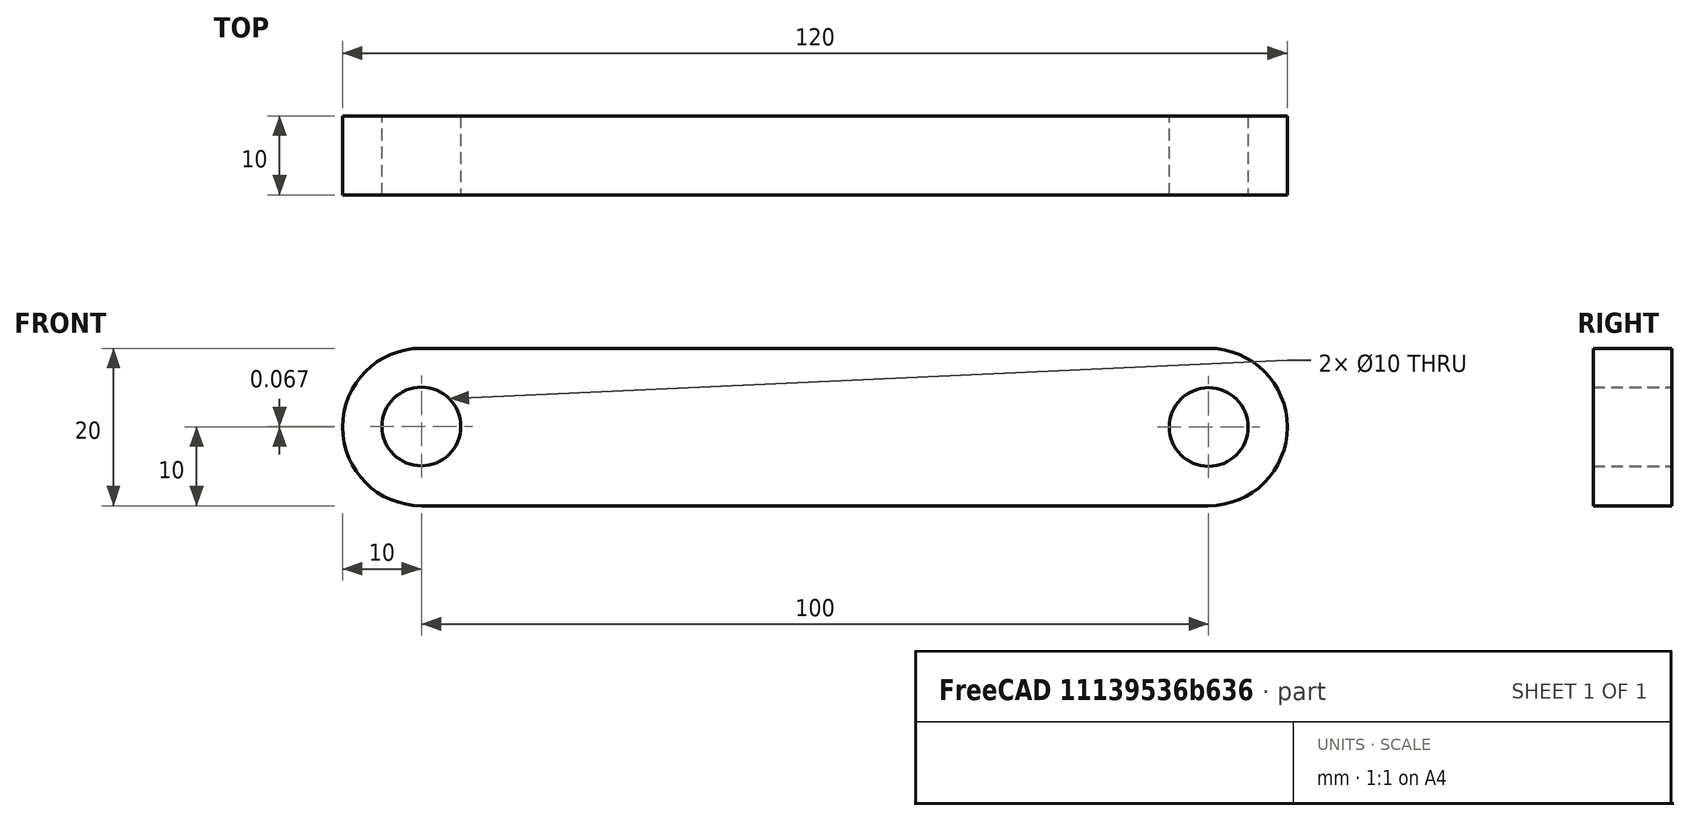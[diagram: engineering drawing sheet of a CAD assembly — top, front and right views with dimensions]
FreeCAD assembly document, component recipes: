
FREECAD ASSEMBLY — COMPONENT RECIPES ("Tuto1-001")

This assembly document has 2 components, labeled P0..P1 below (a component is one placed body or linked part). 1 of them carries a construction recipe — the FreeCAD feature program that regenerates the part from scratch, quoted from this document or its linked companion documents; the rest are supplied as boundary geometry only. No exploded tour is included for this assembly.
COMPONENT P0 — geometry summary ("Assembly"; no construction recipe available for this part):
  bounding box: 187.5 x 79.4 x 10.0 mm
  tessellated surface: 136 triangles
  volume: 269599466671506402234081112596510726420148261437092293409454295054376342095374861194592918402182409975518335451632640503398607845710483601597173416451913632217472958464 mm^3 (181082766403595248414619411153999513566451641439836758546339357627439935496059399929033738820857764264489786219256326956075055065643236738184539001915405754758594560% of its bounding box)
  symmetry: mirror-symmetric across its z mid-plane
COMPONENT P1 — recipe-attached ("Body", modeled in this document).
Construction recipe (the document's own serialized feature program — sketch geometry with constraints, then the solid features built on it; lengths are millimeters unless a unit is written):

FEATURE [PartDesign::CoordinateSystem] LCS_0
  AttacherType = Attacher::AttachEngine3D
  MapMode = 2
  Support = -> [X_Axis001]
FEATURE [Sketcher::SketchObject] Sketch
  FullyConstrained = false
  MapMode = 5
  Placement = pos=(0,0,0) rot=(1,0,0;1.5708rad)
  Support = -> [XZ_Plane001]
  sketch-geometry (6):
    g0: ArcOfCircle CenterX=0 CenterY=0 CenterZ=0 NormalX=0 NormalY=0 NormalZ=1 AngleXU=0 Radius=10 StartAngle=1.5708 EndAngle=4.71239
    g1: ArcOfCircle CenterX=100 CenterY=1.1e-15 CenterZ=0 NormalX=0 NormalY=0 NormalZ=1 AngleXU=0 Radius=10 StartAngle=4.71239 EndAngle=7.85398
    g2: LineSegment StartX=-1.8e-15 StartY=-10 StartZ=0 EndX=100 EndY=-10 EndZ=0
    g3: LineSegment StartX=100 StartY=10 StartZ=0 EndX=7.958e-13 EndY=10 EndZ=0
    g4: Circle CenterX=100 CenterY=1.1e-15 CenterZ=0 NormalX=0 NormalY=0 NormalZ=1 AngleXU=0 Radius=5
    g5: Circle CenterX=0 CenterY=0.067016 CenterZ=0 NormalX=0 NormalY=0 NormalZ=1 AngleXU=0 Radius=5
  constraints (11):
    c: Tangent(g0,g2) = -1.5708
    c: Tangent(g2,g1) = -1.5708
    c: Tangent(g1,g3) = -1.5708
    c: Tangent(g3,g0) = -1.5708
    c: Equal(g0,g1)
    c: Horizontal(g2)
    c: Coincident(g0,g-1)
    c: Coincident(g4,g1)
    c: PointOnObject(g5,g-2)
    c: Radius(g5) = 5
    c: DistanceX(g5,g1) = 100
FEATURE [PartDesign::Pad] Pad
  Direction = (0,-1,-2e-16)
  Length = 10
  Length2 = 10
  Placement = pos=(0,0,0) rot=(1,0,0;1.5708rad)
  Profile = -> Sketch
  ReferenceAxis = -> Sketch [N_Axis]
  Type = 0
FEATURE [PartDesign::Body] Body
  Group = -> [LCS_0,Sketch,Pad]
  Origin = -> Origin001
  Tip = -> Pad
PROVENANCE & LICENSES
A FreeCAD (.FCStd) document from a public repository crawl; recipes are the document's own serialized feature recipes (and, for linked parts, companion documents' recipes).
License: as declared in the source repository (recorded in the dataset sidecar).
